# Revit family: Lavatory_Console-DXV-Oak_Hill-D20155002_D21411030_Series
name_source: partatom
category: Plumbing Fixtures
revit_build: Autodesk Revit 2014 (Build: 20130308_1515(x64)
units: mm (PartAtom-declared; Revit-internal decimal feet)

## types (4) — shared parameters
ADA Compliant = Yes
Assembly Code = D2010310
Basin Finish = Fire Clay-DXV-415-Canvas White
Basin Shape = Rectangular
CW Connection = Yes
CWFU = 1.5
Cold Water Connection Diameter = 1/2"
Cold Water Connection Height = 38 3/4"
Cold Water Connection Radius = 1/4"
Cold Water Connection Width = 4"
Default Elevation = 36"
Description = Oak Hill 30" Lavatory with Console
HW Connection = Yes
HWFU = 1.5
Height = 41 1/16"
Hot Water Connection Diameter = 1"
Hot Water Connection Height = 38 3/4"
Hot Water Connection Radius = 1/4"
Hot Water Connection Width = 4"
Installation Type = Deck Mounted
Length = 22"
Manufacturer = DXV American Standard
Material = Fire Clay-DXV-415-Canvas White
Price = Prices may vary. Please consult Manufacturer Representative for most up-to-date price list.
Product Documentation Link = https://dxv01.blob.core.windows.net
Product Page URL = https://www.dxv.com
URL = http://www.dxv.com
Vent Connection = No
WFU = 2
Warranty Documentation Link = https://www.dxv.com
Waste Connection = Yes
Waste Connection Diameter = 2"
Waste Connection Radius = 1"
Width = 30"

## per-type parameters (varying)
| type | Console Finish |
| D20155002.415_D21411030.100 | Cast Brass-DXV-100-Polished Chrome |
| D20155002.415_D21411030.144 | Cast Brass-DXV-144-Brushed Nickel |
| D20155002.415_D21411030.150 | Cast Brass-DXV-150-Platinum Nickel |
| D20155002.415_D21411030.427 | Cast Brass-DXV-150-Platinum Nickel |

note: column(s) folded — value = type name in every type: Model

## geometry (parser evidence)
native form markers: Sweep x1
no freeform markers — native parametric forms only
